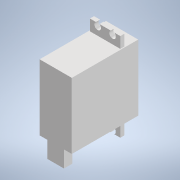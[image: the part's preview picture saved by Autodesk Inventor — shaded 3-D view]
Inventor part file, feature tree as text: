
AUTODESK INVENTOR PART (.ipt)
format: ipt  version: 2022 (Build 260153000, 153)  size: 147,968 bytes
history: native  units: in
note: dims shown in document units (in); Inventor stores cm internally (conversion verified against a paired STEP export)
features: extrude x1, sketch x1, projected_geometry x1
ambient origin geometry x8: Origin, YZ Plane, XZ Plane, XY Plane, X Axis, Y Axis, Z Axis, Center Point
bodies: Solid2 (feature_tree), Solid1 (feature_tree)
feature tree (3):
  extrude  "Extrusion1"  Depth=0.1969in
  sketch  "Sketch1"  dims[d0=0.3937in d1=0.1969in d2=0.3937in d3=0.0in]
  projected_geometry  "Projected Loop1"
